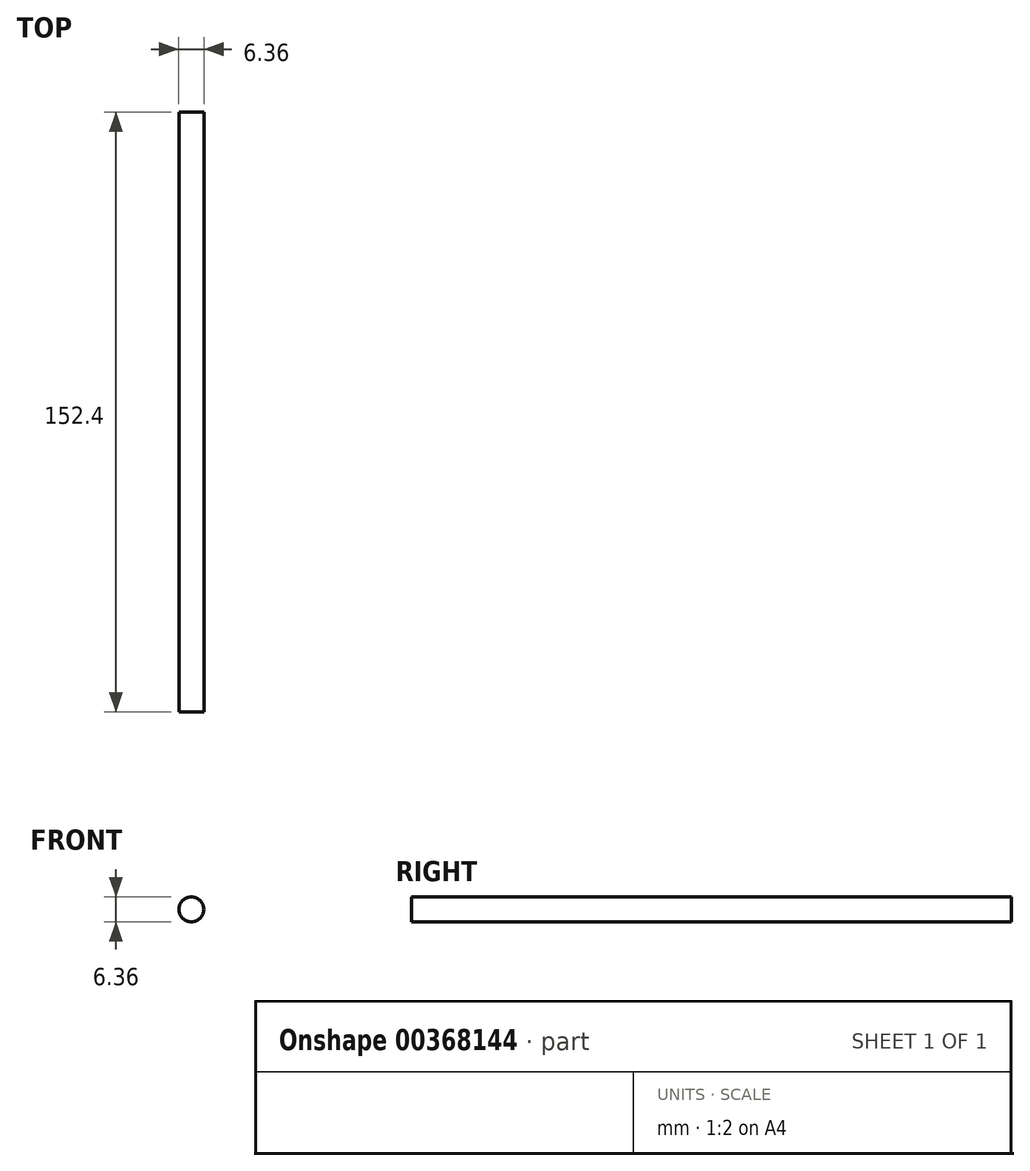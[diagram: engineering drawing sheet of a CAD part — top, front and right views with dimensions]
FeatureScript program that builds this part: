
annotation { "Feature Type Name" : "Feature", "Feature Type Description" : "" }
export const myFeature = defineFeature(function(context is Context, id is Id, definition is map)
    precondition{}
    {
        {
            var Q0;
            Q0=qCreatedBy(makeId("Front.planeOp"),FACE);
            var sketch = newSketch(context, id + "F0", { "sketchPlane" : qUnion([Q0])});
            skCircle(sketch, "E0", {"center": v(0, 0) * mm, "radius": 3.18 * mm});
            skSolve(sketch);
        }
        {
            var Q0;
            Q0=makeQuery(id+"F0.imprint","IMPRINT",FACE,{"disambiguationData":[TD([[makeQuery(id+"F0.imprint","IMPRINT",EDGE,{"derivedFrom":sQuery(id+"F0.wireOp",EDGE,"E0")}),1.0]])]});
            extrude(context, id + "F1", {"entities" : qUnion([Q0]), "depth" : 152.4 * mm, "offsetDistance" : 25.4 * mm});
        }
    });
